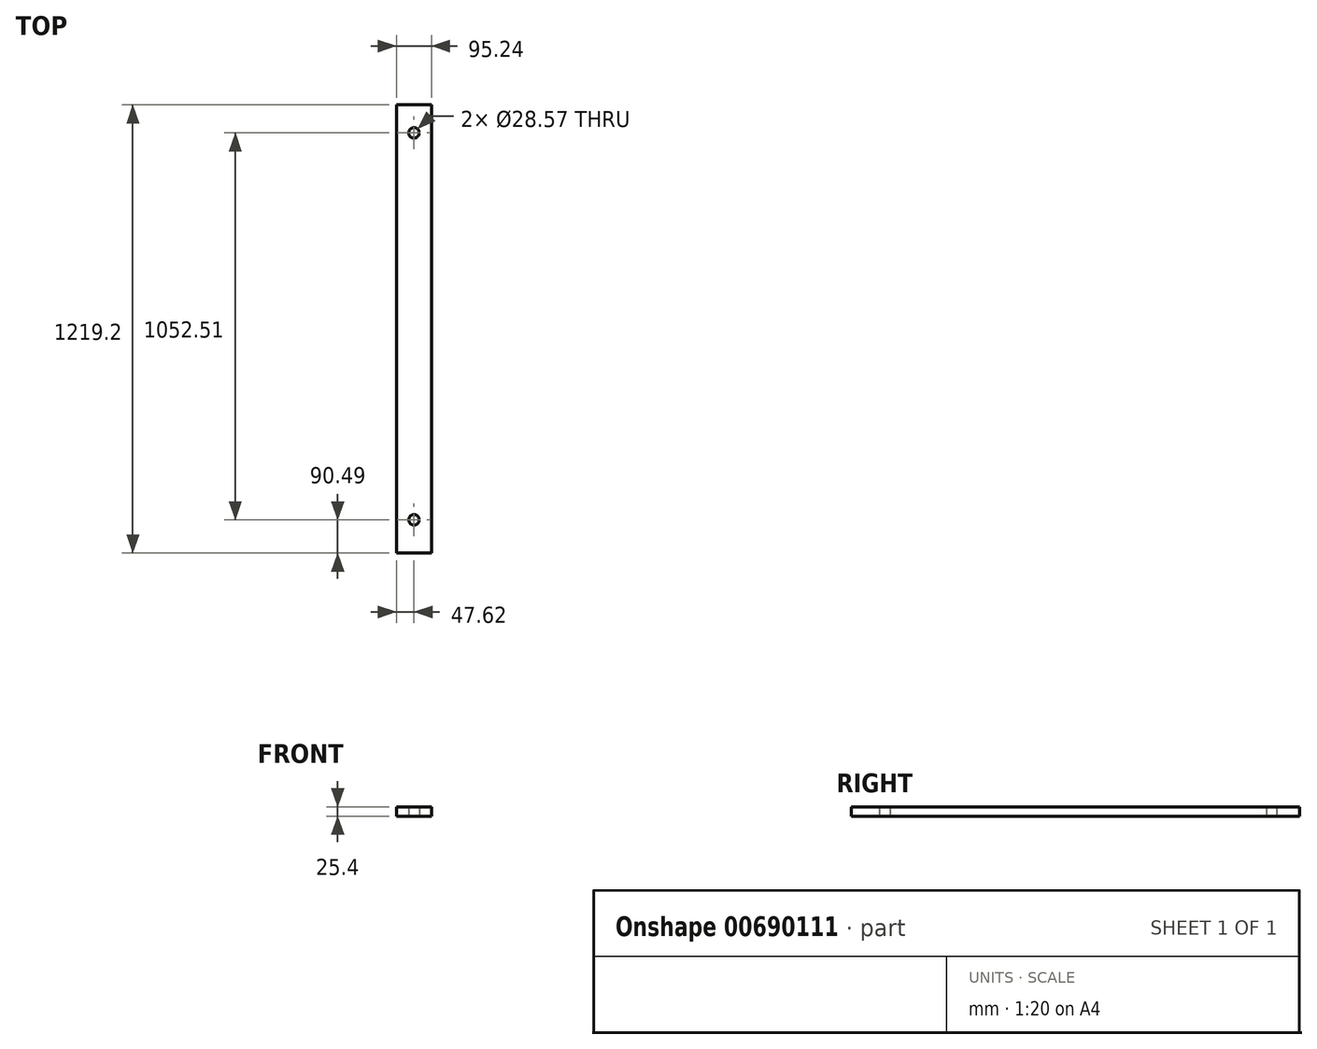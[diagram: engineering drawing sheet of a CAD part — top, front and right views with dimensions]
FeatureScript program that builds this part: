
annotation { "Feature Type Name" : "Feature", "Feature Type Description" : "" }
export const myFeature = defineFeature(function(context is Context, id is Id, definition is map)
    precondition{}
    {
        {
            var Q0;
            Q0=qCreatedBy(makeId("Top.planeOp"),FACE);
            var sketch = newSketch(context, id + "F0", { "sketchPlane" : qUnion([Q0])});
            skLineSegment(sketch, "E0.bottom", {"start": v(-47.63, 116.04) * mm, "end": v(47.63, 116.04) * mm});
            skLineSegment(sketch, "E0.top", {"start": v(-47.62, -1103.16) * mm, "end": v(47.63, -1103.16) * mm});
            skLineSegment(sketch, "E0.left", {"start": v(-47.63, 116.04) * mm, "end": v(-47.62, -1103.16) * mm});
            skLineSegment(sketch, "E0.right", {"start": v(47.63, 116.04) * mm, "end": v(47.63, -1103.16) * mm});
            skCircle(sketch, "E1", {"center": v(0, 39.84) * mm, "radius": 14.29 * mm});
            skCircle(sketch, "E2", {"center": v(0, -1012.67) * mm, "radius": 14.29 * mm});
            skSolve(sketch);
        }
        {
            var Q0;
            Q0 = qSketchRegion(id + "F0", true);
            extrude(context, id + "F1", {"entities" : qUnion([Q0]), "depth" : 25.4 * mm, "offsetDistance" : 25.4 * mm});
        }
    });
